# Revit family: ihf_3d_knx_007607
name_source: partatom
category: Elektroinstallationen
revit_build: Autodesk Revit 2016 (Build: 20190508_0715(x64)
units: mm (PartAtom-declared; Revit-internal decimal feet)

## family parameters
Basisbauteil = Fläche
Beim Laden mit Abzugskörper schneiden = Nein
Bemaßung runder Anschluss = Durchmesser verwenden
Beschriftungsausrichtung beibehalten = Nein
Gemeinsam genutzt = Nein
Raumberechnungspunkt = Nein
Teiletyp = Normal

## types (1)
- iHF 3D KNX
    Apparent Load = 0 VA
    Beschreibung = Type: Motion detectors; Dimensions (L x W x H): 120 x 117 x 120 mm; Power supply, detail: KNX bus; Sensor Technology: iHF (intelligent high-frequency technology); Application, place: Outdoors; Application, room: outdoors, front door, all round the building, terrace / balcony, courtyard & driveway; Installation site: wall; Installation: Surface wiring; HF-system: 5,8 GHz; Electronic scalability: Yes; Mechanical scalability: No; Mounting height: 1,80 – 2,00 m; Optimum mounting height: 1,8 m; Detection angle: 160 °; Angle of aperture: 100 °; Sneak-by guard: Yes; Reach, detail: Detection zone adjustable on 3 axes; Reach, radial: r = 7 m (68 m²); Reach, tangential: r = 7 m (68 m²); Twilight setting TEACH: Yes; Twilight setting: 2 – 2000 lx; Time setting: 60 sec – 255 min; Basic light level function: Yes; KNX functions: Light output 1x, Presence output, Light level, Basic light level function, Photo-cell controller, Direction of movement, Distance; With bus coupling: Yes; Settings via: ETS software, Remote control, Bus, Smart Remote; With remote control: Yes; IP-rating: IP54; Material: Plastic; Ambient temperature: -20 – 50 °C; Colour: white; Colour, RAL: 9010; Manufacturer's Warranty: 5 years; Version: white; PU1, EAN: 4007841007607
    Height = 120 mm  [stored 0.393701 ft]
    Hersteller = Steinel
    Length = 120 mm  [stored 0.393701 ft]
    Maximum range = 6.431 m
    ModVariant = Nein
    Modell = 007607
    Mounting Type = Surface mounted
    Number of Poles = 1
    OnlyDefault = Ja
    Power Factor = 1
    Product Name = iHF 3D KNX
    Product group = Sensor-switched indoor light
    ProductGroupID = 30
    Protection Class = Protection class
    Protection Degree = IP 54
    RlxData = <blob elided: 142973 chars, md5=468cb199>
    Sensor characteristics = Semi circular 145°-300°
    Sensor type = HF
    SensorDataFile = <blob elided: 144225 chars, md5=4f57d913>
    Type of entry = Motion
    Typenbild = produkt1_007607.jpg
    Typenkommentare = Product without accessories
    URL = http://relux.com
    VarID = ---
    Voltage = 0 V
    Vorgabe-Ansicht = 1800 mm
    Weight = 0.00 kg
    Width = 117 mm

note: [stored X ft] marks values corroborated as IEEE doubles in the binary element streams (Revit-internal decimal feet)

## geometry (parser evidence)
native form markers: Blend x4, Sweep x15
no freeform markers — native parametric forms only
